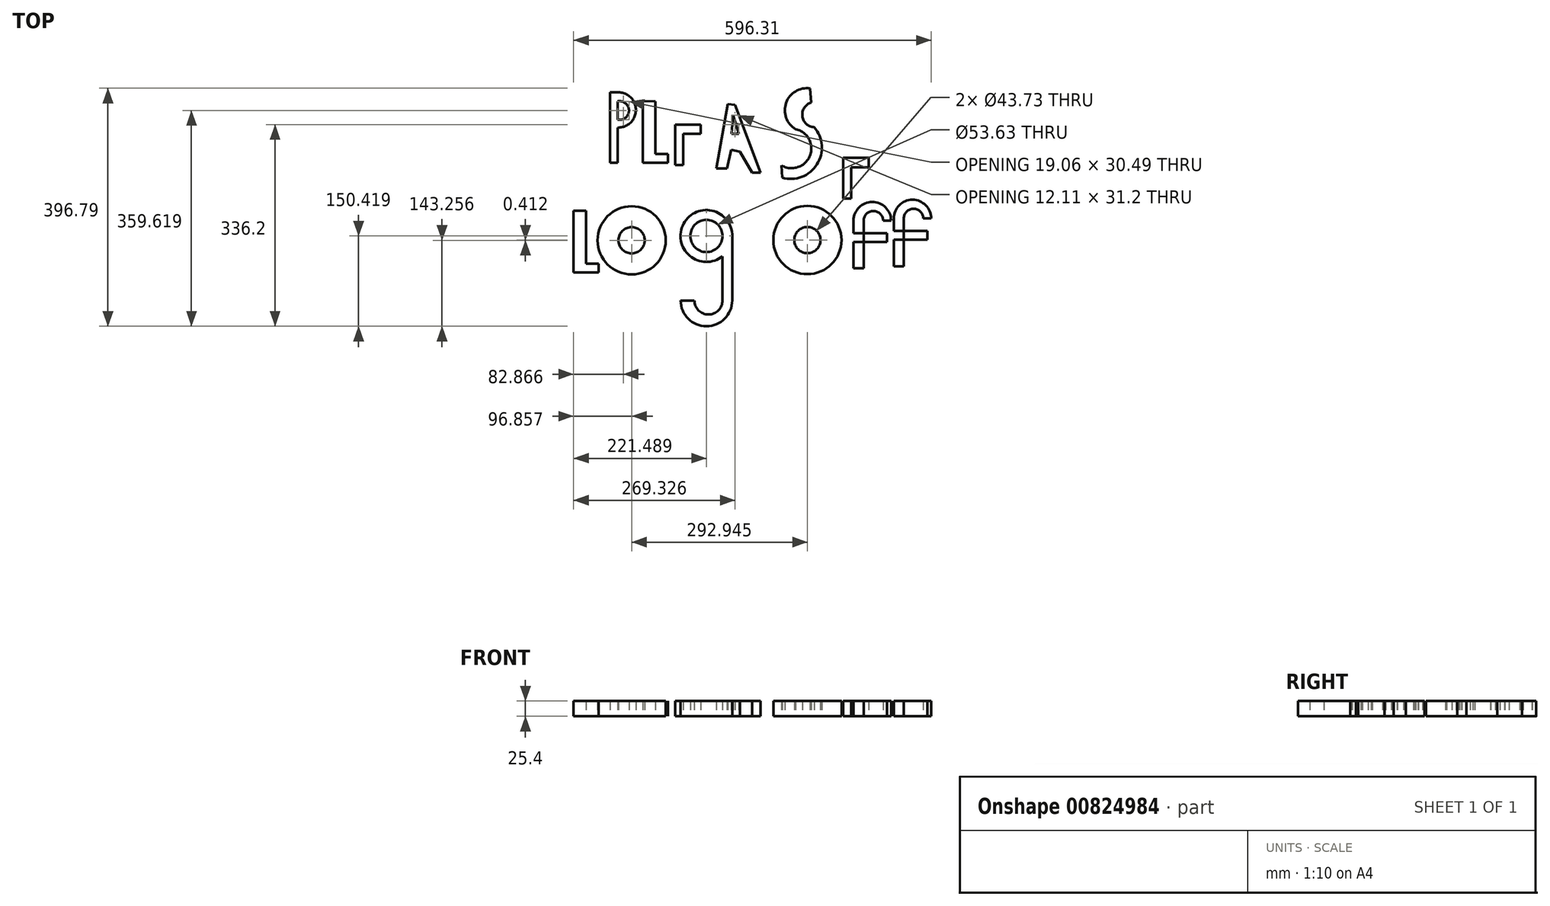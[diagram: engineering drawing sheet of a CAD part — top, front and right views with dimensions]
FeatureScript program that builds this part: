
annotation { "Feature Type Name" : "Feature", "Feature Type Description" : "" }
export const myFeature = defineFeature(function(context is Context, id is Id, definition is map)
    precondition{}
    {
        {
            var Q0;
            Q0=qCreatedBy(makeId("Top.planeOp"),FACE);
            var sketch = newSketch(context, id + "F0", { "sketchPlane" : qUnion([Q0])});
            skLineSegment(sketch, "E0", {"start": v(-63.23, 53.57) * mm, "end": v(-63.23, -63.68) * mm});
            skArc(sketch, "E1", {"start": v(-63.23, -5.06) * mm, "mid": v(-32.66, 24.26) * mm, "end": v(-63.23, 53.57) * mm});
            skLineSegment(sketch, "E2", {"start": v(-21.08, 39) * mm, "end": v(-21.08, -64.1) * mm});
            skLineSegment(sketch, "E3", {"start": v(-21.08, -64.1) * mm, "end": v(20.62, -64.1) * mm});
            skLineSegment(sketch, "E4", {"start": v(32.97, 36.81) * mm, "end": v(32.97, -67.57) * mm});
            skLineSegment(sketch, "E5", {"start": v(32.97, -67.57) * mm, "end": v(79.1, -67.57) * mm});
            skLineSegment(sketch, "E6", {"start": v(32.97, -15.38) * mm, "end": v(75.28, -15.38) * mm});
            skLineSegment(sketch, "E7", {"start": v(32.97, 36.81) * mm, "end": v(76.33, 36.81) * mm});
            skLineSegment(sketch, "E8", {"start": v(120.5, 34.02) * mm, "end": v(101.19, -73.14) * mm});
            skLineSegment(sketch, "E9", {"start": v(101.19, -73.14) * mm, "end": v(119.24, -73.14) * mm});
            skLineSegment(sketch, "E10", {"start": v(119.24, -73.14) * mm, "end": v(126.45, -41.96) * mm});
            skLineSegment(sketch, "E11", {"start": v(126.45, -41.96) * mm, "end": v(141.1, -45.34) * mm});
            skLineSegment(sketch, "E12", {"start": v(141.1, -45.34) * mm, "end": v(160.93, -80.13) * mm});
            skLineSegment(sketch, "E13", {"start": v(160.93, -80.13) * mm, "end": v(175.4, -80.13) * mm});
            skLineSegment(sketch, "E14", {"start": v(175.4, -80.13) * mm, "end": v(132.54, 32.67) * mm});
            skLineSegment(sketch, "E15", {"start": v(132.54, 32.67) * mm, "end": v(120.5, 34.02) * mm});
            skLineSegment(sketch, "E16", {"start": v(126.71, -15.73) * mm, "end": v(138.82, -15.73) * mm});
            skLineSegment(sketch, "E17", {"start": v(138.82, -15.73) * mm, "end": v(129.44, 15.47) * mm});
            skLineSegment(sketch, "E18", {"start": v(129.44, 15.47) * mm, "end": v(126.71, -15.73) * mm});
            skLineSegment(sketch, "E19", {"start": v(75.28, -15.38) * mm, "end": v(75.28, 0) * mm});
            skLineSegment(sketch, "E20", {"start": v(75.28, 0) * mm, "end": v(32.97, 0) * mm});
            skLineSegment(sketch, "E21", {"start": v(32.97, 0) * mm, "end": v(45.74, 0) * mm});
            skLineSegment(sketch, "E22", {"start": v(45.74, 0) * mm, "end": v(45.74, 36.81) * mm});
            skLineSegment(sketch, "E23", {"start": v(45.74, 36.81) * mm, "end": v(45.74, 28.08) * mm});
            skLineSegment(sketch, "E24", {"start": v(45.74, 28.08) * mm, "end": v(75.28, 28.08) * mm});
            skLineSegment(sketch, "E25", {"start": v(75.28, 28.08) * mm, "end": v(76.33, 36.81) * mm});
            skLineSegment(sketch, "E26", {"start": v(46.18, -15.38) * mm, "end": v(46.18, -67.57) * mm});
            skPoint(sketch, "E26.endSnap0", {"position": v(56.03, -67.57) * mm});
            skLineSegment(sketch, "E27", {"start": v(46.18, -67.57) * mm, "end": v(46.18, -51.22) * mm});
            skLineSegment(sketch, "E28", {"start": v(46.18, -51.22) * mm, "end": v(79.33, -51.22) * mm});
            skLineSegment(sketch, "E29", {"start": v(79.33, -51.22) * mm, "end": v(79.1, -67.57) * mm});
            skLineSegment(sketch, "E30", {"start": v(20.62, -64.1) * mm, "end": v(20.62, -49.31) * mm});
            skLineSegment(sketch, "E31", {"start": v(20.62, -49.31) * mm, "end": v(0, -49.31) * mm});
            skLineSegment(sketch, "E32", {"start": v(0, -49.31) * mm, "end": v(0, 38.42) * mm});
            skLineSegment(sketch, "E33", {"start": v(0, 38.42) * mm, "end": v(-21.08, 39) * mm});
            skLineSegment(sketch, "E34", {"start": v(-63.23, -63.68) * mm, "end": v(-75.7, -64.1) * mm});
            skLineSegment(sketch, "E35", {"start": v(-75.7, -64.1) * mm, "end": v(-75.7, 53.63) * mm});
            skLineSegment(sketch, "E36", {"start": v(-75.7, 53.63) * mm, "end": v(-63.23, 53.57) * mm});
            skLineSegment(sketch, "E37", {"start": v(313.15, -18.97) * mm, "end": v(313.15, -123.35) * mm});
            skLineSegment(sketch, "E38", {"start": v(313.15, -123.35) * mm, "end": v(359.28, -123.35) * mm});
            skLineSegment(sketch, "E39", {"start": v(313.15, -71.16) * mm, "end": v(355.46, -71.16) * mm});
            skLineSegment(sketch, "E40", {"start": v(313.15, -18.97) * mm, "end": v(356.5, -18.97) * mm});
            skLineSegment(sketch, "E41", {"start": v(355.46, -71.16) * mm, "end": v(355.46, -55.79) * mm});
            skLineSegment(sketch, "E42", {"start": v(355.46, -55.79) * mm, "end": v(313.15, -55.79) * mm});
            skLineSegment(sketch, "E43", {"start": v(313.15, -55.79) * mm, "end": v(325.91, -55.79) * mm});
            skLineSegment(sketch, "E44", {"start": v(325.91, -55.79) * mm, "end": v(325.91, -18.97) * mm});
            skLineSegment(sketch, "E45", {"start": v(325.91, -18.97) * mm, "end": v(325.91, -27.7) * mm});
            skLineSegment(sketch, "E46", {"start": v(325.91, -27.7) * mm, "end": v(355.46, -27.7) * mm});
            skLineSegment(sketch, "E47", {"start": v(355.46, -27.7) * mm, "end": v(356.5, -18.97) * mm});
            skLineSegment(sketch, "E48", {"start": v(326.36, -71.16) * mm, "end": v(326.36, -123.35) * mm});
            skPoint(sketch, "E48.endSnap0", {"position": v(336.21, -123.35) * mm});
            skLineSegment(sketch, "E49", {"start": v(326.36, -123.35) * mm, "end": v(326.36, -107) * mm});
            skLineSegment(sketch, "E50", {"start": v(326.36, -107) * mm, "end": v(359.51, -107) * mm});
            skLineSegment(sketch, "E51", {"start": v(359.51, -107) * mm, "end": v(359.28, -123.35) * mm});
            skLineSegment(sketch, "E52", {"start": v(-136.56, -143.5) * mm, "end": v(-136.56, -246.6) * mm});
            skLineSegment(sketch, "E53", {"start": v(-136.56, -246.6) * mm, "end": v(-94.85, -246.6) * mm});
            skLineSegment(sketch, "E54", {"start": v(-94.85, -246.6) * mm, "end": v(-94.85, -231.81) * mm});
            skLineSegment(sketch, "E55", {"start": v(-94.85, -231.81) * mm, "end": v(-115.48, -231.81) * mm});
            skLineSegment(sketch, "E56", {"start": v(-115.48, -231.81) * mm, "end": v(-115.48, -144.08) * mm});
            skLineSegment(sketch, "E57", {"start": v(-115.48, -144.08) * mm, "end": v(-136.56, -143.5) * mm});
            skCircle(sketch, "E58", {"center": v(-39.7, -193.07) * mm, "radius": 56.82 * mm});
            skCircle(sketch, "E59", {"center": v(-39.7, -193.07) * mm, "radius": 21.87 * mm});
            skCircle(sketch, "E60", {"center": v(84.93, -185.91) * mm, "radius": 43.2 * mm});
            skCircle(sketch, "E61", {"center": v(84.93, -185.91) * mm, "radius": 26.82 * mm});
            skLineSegment(sketch, "E62.bottom", {"start": v(111.75, -185.91) * mm, "end": v(127.9, -185.91) * mm});
            skLineSegment(sketch, "E62.top", {"start": v(111.75, -293.35) * mm, "end": v(127.9, -293.35) * mm});
            skLineSegment(sketch, "E62.left", {"start": v(111.75, -185.91) * mm, "end": v(111.75, -293.35) * mm});
            skLineSegment(sketch, "E62.right", {"start": v(127.9, -185.91) * mm, "end": v(127.9, -293.35) * mm});
            skArc(sketch, "E63", {"start": v(64.87, -293.35) * mm, "mid": v(88.3, -316.79) * mm, "end": v(111.75, -293.35) * mm});
            skArc(sketch, "E64", {"start": v(41.95, -293.35) * mm, "mid": v(84.93, -336.33) * mm, "end": v(127.9, -293.35) * mm});
            skLineSegment(sketch, "E65", {"start": v(41.95, -293.35) * mm, "end": v(64.87, -293.35) * mm});
            skCircle(sketch, "E66", {"center": v(253.24, -192.66) * mm, "radius": 56.82 * mm});
            skCircle(sketch, "E67", {"center": v(253.24, -192.66) * mm, "radius": 21.87 * mm});
            skLineSegment(sketch, "E68.bottom", {"start": v(330.15, -239.8) * mm, "end": v(346.97, -239.8) * mm});
            skLineSegment(sketch, "E68.top", {"start": v(330.15, -160.39) * mm, "end": v(346.97, -160.39) * mm});
            skLineSegment(sketch, "E68.left", {"start": v(330.15, -239.8) * mm, "end": v(330.15, -160.39) * mm});
            skLineSegment(sketch, "E68.right", {"start": v(346.97, -239.8) * mm, "end": v(346.97, -160.39) * mm});
            skLineSegment(sketch, "E69.bottom", {"start": v(330.15, -180.94) * mm, "end": v(386.21, -180.94) * mm});
            skLineSegment(sketch, "E69.top", {"start": v(330.15, -195.9) * mm, "end": v(386.21, -195.9) * mm});
            skLineSegment(sketch, "E69.left", {"start": v(330.15, -180.94) * mm, "end": v(330.15, -195.9) * mm});
            skLineSegment(sketch, "E69.right", {"start": v(386.21, -180.94) * mm, "end": v(386.21, -195.9) * mm});
            skArc(sketch, "E70", {"start": v(392.75, -160.39) * mm, "mid": v(361.45, -129.1) * mm, "end": v(330.15, -160.39) * mm});
            skArc(sketch, "E71", {"start": v(379.44, -160.39) * mm, "mid": v(363.2, -144.15) * mm, "end": v(346.97, -160.39) * mm});
            skLineSegment(sketch, "E72", {"start": v(379.44, -160.39) * mm, "end": v(392.75, -160.39) * mm});
            skPoint(sketch, "E73.endSnap0", {"position": v(403.21, -119.74) * mm});
            skLineSegment(sketch, "E74.bottom", {"start": v(397.15, -236.2) * mm, "end": v(413.97, -236.2) * mm});
            skLineSegment(sketch, "E74.top", {"start": v(397.15, -156.78) * mm, "end": v(413.97, -156.78) * mm});
            skLineSegment(sketch, "E74.left", {"start": v(397.15, -236.2) * mm, "end": v(397.15, -156.78) * mm});
            skLineSegment(sketch, "E74.right", {"start": v(413.97, -236.2) * mm, "end": v(413.97, -156.78) * mm});
            skLineSegment(sketch, "E75.bottom", {"start": v(397.15, -177.33) * mm, "end": v(453.2, -177.33) * mm});
            skLineSegment(sketch, "E75.top", {"start": v(397.15, -192.28) * mm, "end": v(453.2, -192.28) * mm});
            skLineSegment(sketch, "E75.left", {"start": v(397.15, -177.33) * mm, "end": v(397.15, -192.28) * mm});
            skLineSegment(sketch, "E75.right", {"start": v(453.2, -177.33) * mm, "end": v(453.2, -192.28) * mm});
            skArc(sketch, "E76", {"start": v(459.75, -156.78) * mm, "mid": v(428.45, -125.48) * mm, "end": v(397.15, -156.78) * mm});
            skArc(sketch, "E77", {"start": v(446.44, -156.78) * mm, "mid": v(430.2, -140.54) * mm, "end": v(413.97, -156.78) * mm});
            skLineSegment(sketch, "E78", {"start": v(446.44, -156.78) * mm, "end": v(459.75, -156.78) * mm});
            skArc(sketch, "E79", {"start": v(-63.23, 8.04) * mm, "mid": v(-44.16, 23.29) * mm, "end": v(-63.23, 38.53) * mm});
            skPoint(sketch, "E80.center.orphan", {"position": v(224.65, -10.5) * mm});
            skPoint(sketch, "E81.start.orphan", {"position": v(224.65, 4.32) * mm});
            skArc(sketch, "E82", {"start": v(257.75, 60.05) * mm, "mid": v(217.78, 36.12) * mm, "end": v(233.63, -7.7) * mm});
            skArc(sketch, "E83", {"start": v(210.02, -68.25) * mm, "mid": v(257.5, -51.88) * mm, "end": v(233.63, -7.7) * mm});
            skLineSegment(sketch, "E84", {"start": v(257.75, 60.05) * mm, "end": v(259.7, 36.66) * mm});
            skArc(sketch, "E85", {"start": v(259.7, 36.66) * mm, "mid": v(244.8, 14.05) * mm, "end": v(264.42, -4.61) * mm});
            skLineSegment(sketch, "E86", {"start": v(210.02, -68.25) * mm, "end": v(211.05, -88.78) * mm});
            skArc(sketch, "E87", {"start": v(211.05, -88.78) * mm, "mid": v(269.17, -66.63) * mm, "end": v(264.42, -4.61) * mm});
            skSolve(sketch);
        }
        {
            var Q0;
            Q0=makeQuery(id+"F0.imprint","IMPRINT",FACE,{"disambiguationData":[TD([[makeQuery(id+"F0.imprint","IMPRINT",EDGE,{"derivedFrom":sQuery(id+"F0.wireOp",EDGE,"E2")}),1.0]])]});
            var Q1;
            Q1=makeQuery(id+"F0.imprint","IMPRINT",FACE,{"disambiguationData":[TD([[makeQuery(id+"F0.imprint","IMPRINT",EDGE,{"derivedFrom":sQuery(id+"F0.wireOp",EDGE,"E80")}),1.0]])]});
            var Q2;
            Q2=makeQuery(id+"F0.imprint","IMPRINT",FACE,{"disambiguationData":[TD([[makeQuery(id+"F0.imprint","IMPRINT",EDGE,{"derivedFrom":sQuery(id+"F0.wireOp",EDGE,"E52")}),1.0]])]});
            var Q3;
            {var subQ0=sQuery(id+"F0.wireOp",EDGE,"E1");Q3=makeQuery(id+"F0.imprint","IMPRINT",FACE,{"disambiguationData":[TD([[makeQuery(id+"F0.imprint","IMPRINT",EDGE,{"derivedFrom":subQ0}),1.0]])]});}
            var Q4;
            {var subQ2=sQuery(id+"F0.wireOp",EDGE,"E27");Q4=makeQuery(id+"F0.imprint","IMPRINT",FACE,{"disambiguationData":[TD([[makeQuery(id+"F0.imprint","IMPRINT",EDGE,{"derivedFrom":subQ2}),-1.0]])]});}
            var Q5;
            {var subQ2=sQuery(id+"F0.wireOp",EDGE,"E23");Q5=makeQuery(id+"F0.imprint","IMPRINT",FACE,{"disambiguationData":[TD([[makeQuery(id+"F0.imprint","IMPRINT",EDGE,{"derivedFrom":subQ2}),1.0]])]});}
            var Q6;
            Q6=makeQuery(id+"F0.imprint","IMPRINT",FACE,{"disambiguationData":[TD([[makeQuery(id+"F0.imprint","IMPRINT",EDGE,{"derivedFrom":sQuery(id+"F0.wireOp",EDGE,"E8")}),1.0]])]});
            var Q7;
            {var subQ2=sQuery(id+"F0.wireOp",EDGE,"E49");Q7=makeQuery(id+"F0.imprint","IMPRINT",FACE,{"disambiguationData":[TD([[makeQuery(id+"F0.imprint","IMPRINT",EDGE,{"derivedFrom":subQ2}),-1.0]])]});}
            var Q8;
            {var subQ2=sQuery(id+"F0.wireOp",EDGE,"E45");Q8=makeQuery(id+"F0.imprint","IMPRINT",FACE,{"disambiguationData":[TD([[makeQuery(id+"F0.imprint","IMPRINT",EDGE,{"derivedFrom":subQ2}),1.0]])]});}
            var Q9;
            Q9=makeQuery(id+"F0.imprint","IMPRINT",FACE,{"disambiguationData":[TD([[makeQuery(id+"F0.imprint","IMPRINT",EDGE,{"derivedFrom":sQuery(id+"F0.wireOp",EDGE,"E58")}),1.0]])]});
            var Q10;
            Q10=makeQuery(id+"F0.imprint","IMPRINT",FACE,{"disambiguationData":[TD([[makeQuery(id+"F0.imprint","IMPRINT",EDGE,{"derivedFrom":sQuery(id+"F0.wireOp",EDGE,"E62.top")}),-1.0]])]});
            var Q11;
            Q11=makeQuery(id+"F0.imprint","IMPRINT",FACE,{"disambiguationData":[TD([[makeQuery(id+"F0.imprint","IMPRINT",EDGE,{"derivedFrom":sQuery(id+"F0.wireOp",EDGE,"E66")}),1.0]])]});
            var Q12;
            {var subQ0=sQuery(id+"F0.wireOp",EDGE,"E68.bottom");Q12=makeQuery(id+"F0.imprint","IMPRINT",FACE,{"disambiguationData":[TD([[makeQuery(id+"F0.imprint","IMPRINT",EDGE,{"derivedFrom":subQ0}),1.0]])]});}
            var Q13;
            Q13=makeQuery(id+"F0.imprint","IMPRINT",FACE,{"disambiguationData":[TD([[makeQuery(id+"F0.imprint","IMPRINT",EDGE,{"derivedFrom":sQuery(id+"F0.wireOp",EDGE,"E68.top")}),1.0]])]});
            var Q14;
            {var subQ5=sQuery(id+"F0.wireOp",EDGE,"E69.right");Q14=makeQuery(id+"F0.imprint","IMPRINT",FACE,{"disambiguationData":[TD([[makeQuery(id+"F0.imprint","IMPRINT",EDGE,{"derivedFrom":subQ5}),-1.0]])]});}
            var Q15;
            {var subQ0=sQuery(id+"F0.wireOp",EDGE,"E74.bottom");Q15=makeQuery(id+"F0.imprint","IMPRINT",FACE,{"disambiguationData":[TD([[makeQuery(id+"F0.imprint","IMPRINT",EDGE,{"derivedFrom":subQ0}),1.0]])]});}
            var Q16;
            Q16=makeQuery(id+"F0.imprint","IMPRINT",FACE,{"disambiguationData":[TD([[makeQuery(id+"F0.imprint","IMPRINT",EDGE,{"derivedFrom":sQuery(id+"F0.wireOp",EDGE,"E74.top")}),1.0]])]});
            var Q17;
            {var subQ5=sQuery(id+"F0.wireOp",EDGE,"E75.right");Q17=makeQuery(id+"F0.imprint","IMPRINT",FACE,{"disambiguationData":[TD([[makeQuery(id+"F0.imprint","IMPRINT",EDGE,{"derivedFrom":subQ5}),-1.0]])]});}
            var Q18;
            {var subQ0=sQuery(id+"F0.wireOp",EDGE,"E21");Q18=makeQuery(id+"F0.imprint","IMPRINT",FACE,{"disambiguationData":[TD([[makeQuery(id+"F0.imprint","IMPRINT",EDGE,{"derivedFrom":subQ0}),1.0]])]});}
            var Q19;
            {var subQ0=sQuery(id+"F0.wireOp",EDGE,"E19");Q19=makeQuery(id+"F0.imprint","IMPRINT",FACE,{"disambiguationData":[TD([[makeQuery(id+"F0.imprint","IMPRINT",EDGE,{"derivedFrom":subQ0}),1.0]])]});}
            var Q20;
            {var subQ3=sQuery(id+"F0.wireOp",EDGE,"E26");Q20=makeQuery(id+"F0.imprint","IMPRINT",FACE,{"disambiguationData":[TD([[makeQuery(id+"F0.imprint","IMPRINT",EDGE,{"derivedFrom":subQ3}),-1.0]])]});}
            var Q21;
            {var subQ0=sQuery(id+"F0.wireOp",EDGE,"E43");Q21=makeQuery(id+"F0.imprint","IMPRINT",FACE,{"disambiguationData":[TD([[makeQuery(id+"F0.imprint","IMPRINT",EDGE,{"derivedFrom":subQ0}),1.0]])]});}
            var Q22;
            {var subQ0=sQuery(id+"F0.wireOp",EDGE,"E41");Q22=makeQuery(id+"F0.imprint","IMPRINT",FACE,{"disambiguationData":[TD([[makeQuery(id+"F0.imprint","IMPRINT",EDGE,{"derivedFrom":subQ0}),1.0]])]});}
            var Q23;
            {var subQ0=sQuery(id+"F0.wireOp",EDGE,"E48");Q23=makeQuery(id+"F0.imprint","IMPRINT",FACE,{"disambiguationData":[TD([[makeQuery(id+"F0.imprint","IMPRINT",EDGE,{"derivedFrom":subQ0}),-1.0]])]});}
            var Q24;
            {var subQ5=sQuery(id+"F0.wireOp",EDGE,"E62.bottom");Q24=makeQuery(id+"F0.imprint","IMPRINT",FACE,{"disambiguationData":[TD([[makeQuery(id+"F0.imprint","IMPRINT",EDGE,{"derivedFrom":subQ5}),-1.0]])]});}
            var Q25;
            {var subQ5=sQuery(id+"F0.wireOp",EDGE,"E62.top");Q25=makeQuery(id+"F0.imprint","IMPRINT",FACE,{"disambiguationData":[TD([[makeQuery(id+"F0.imprint","IMPRINT",EDGE,{"derivedFrom":subQ5}),1.0]])]});}
            var Q26;
            {var subQ2=sQuery(id+"F0.wireOp",EDGE,"E61");Q26=makeQuery(id+"F0.imprint","IMPRINT",FACE,{"disambiguationData":[TD([[makeQuery(id+"F0.imprint","IMPRINT",EDGE,{"derivedFrom":subQ2}),-1.0]])]});}
            var Q27;
            {var subQ0=sQuery(id+"F0.wireOp",EDGE,"E68.top");Q27=makeQuery(id+"F0.imprint","IMPRINT",FACE,{"disambiguationData":[TD([[makeQuery(id+"F0.imprint","IMPRINT",EDGE,{"derivedFrom":subQ0}),-1.0]])]});}
            var Q28;
            {var subQ0=sQuery(id+"F0.wireOp",EDGE,"E74.top");Q28=makeQuery(id+"F0.imprint","IMPRINT",FACE,{"disambiguationData":[TD([[makeQuery(id+"F0.imprint","IMPRINT",EDGE,{"derivedFrom":subQ0}),-1.0]])]});}
            var Q29;
            {var subQ5=sQuery(id+"F0.wireOp",EDGE,"E69.left");Q29=makeQuery(id+"F0.imprint","IMPRINT",FACE,{"disambiguationData":[TD([[makeQuery(id+"F0.imprint","IMPRINT",EDGE,{"derivedFrom":subQ5}),1.0]])]});}
            var Q30;
            {var subQ5=sQuery(id+"F0.wireOp",EDGE,"E75.left");Q30=makeQuery(id+"F0.imprint","IMPRINT",FACE,{"disambiguationData":[TD([[makeQuery(id+"F0.imprint","IMPRINT",EDGE,{"derivedFrom":subQ5}),1.0]])]});}
            var Q31;
            {var subQ0=sQuery(id+"F0.wireOp",EDGE,"E34");Q31=makeQuery(id+"F0.imprint","IMPRINT",FACE,{"disambiguationData":[TD([[makeQuery(id+"F0.imprint","IMPRINT",EDGE,{"derivedFrom":subQ0}),-1.0]])]});}
            var Q32;
            Q32=makeQuery(id+"F0.imprint","IMPRINT",FACE,{"disambiguationData":[TD([[makeQuery(id+"F0.imprint","IMPRINT",EDGE,{"derivedFrom":sQuery(id+"F0.wireOp",EDGE,"E82")}),1.0]])]});
            extrude(context, id + "F1", {"entities" : qUnion([Q0, Q1, Q2, Q3, Q4, Q5, Q6, Q7, Q8, Q9, Q10, Q11, Q12, Q13, Q14, Q15, Q16, Q17, Q18, Q19, Q20, Q21, Q22, Q23, Q24, Q25, Q26, Q27, Q28, Q29, Q30, Q31, Q32]), "depth" : 25.4 * mm, "offsetDistance" : 25.4 * mm});
        }
    });
